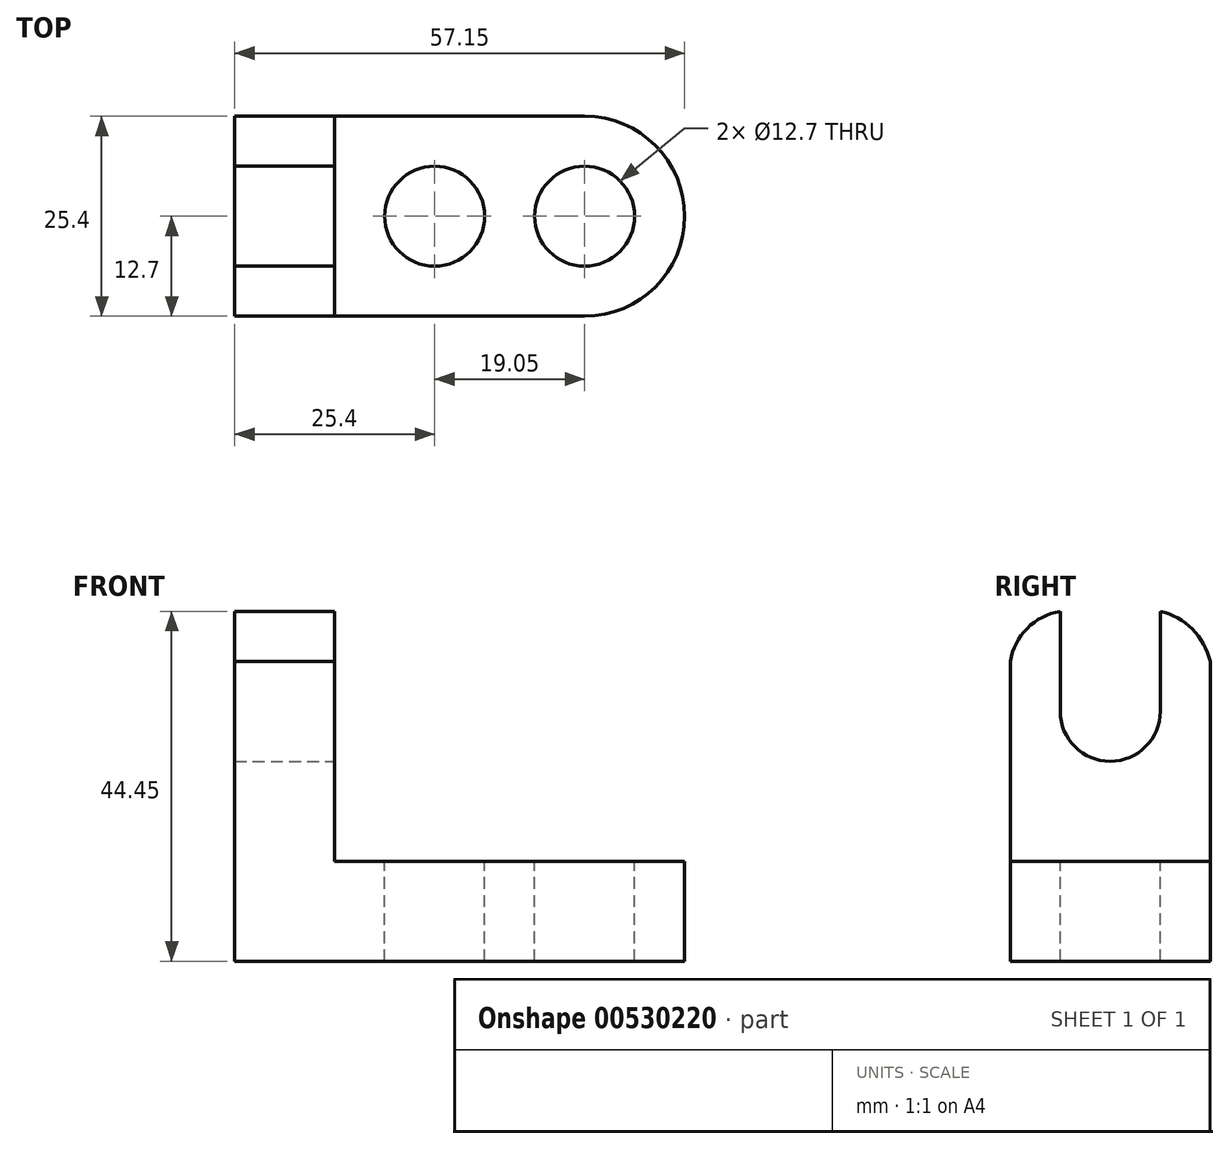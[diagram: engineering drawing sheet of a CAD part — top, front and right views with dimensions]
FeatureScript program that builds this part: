
annotation { "Feature Type Name" : "Feature", "Feature Type Description" : "" }
export const myFeature = defineFeature(function(context is Context, id is Id, definition is map)
    precondition{}
    {
        {
            var Q0;
            Q0=qCreatedBy(makeId("Front.planeOp"),FACE);
            var sketch = newSketch(context, id + "F0", { "sketchPlane" : qUnion([Q0])});
            skLineSegment(sketch, "E0", {"start": v(0, 0) * mm, "end": v(-44.45, 0) * mm});
            skLineSegment(sketch, "E1", {"start": v(-44.45, 0) * mm, "end": v(-44.45, 12.7) * mm});
            skLineSegment(sketch, "E2", {"start": v(-44.45, 12.7) * mm, "end": v(0, 12.7) * mm});
            skLineSegment(sketch, "E3", {"start": v(0, 12.7) * mm, "end": v(0, 0) * mm});
            skSolve(sketch);
        }
        {
            var Q0;
            Q0 = qSketchRegion(id + "F0", true);
            extrude(context, id + "F1", {"entities" : qUnion([Q0]), "depth" : 25.4 * mm, "offsetDistance" : 25.4 * mm});
        }
        {
            var Q0;
            Q0=makeQuery(id+"F1.opExtrude","SWEPT_FACE",FACE,{"disambiguationData":[OSD([sQuery(id+"F0.wireOp",EDGE,"E2")])]});
            var sketch = newSketch(context, id + "F2", { "sketchPlane" : qUnion([Q0])});
            skArc(sketch, "E4", {"start": v(0, -25.4) * mm, "mid": v(12.7, -12.7) * mm, "end": v(0, 0) * mm});
            skSolve(sketch);
        }
        {
            var Q0;
            Q0 = qSketchRegion(id + "F2", true);
            var Q1;
            Q1=makeQuery(id+"F2.imprint","IMPRINT",FACE,{"disambiguationData":[TD([[makeQuery(id+"F2.imprint","IMPRINT",EDGE,{"derivedFrom":sQuery(id+"F2.wireOp",EDGE,"E4")}),1.0]])]});
            extrude(context, id + "F3", {"entities" : qUnion([Q0, Q1]), "operationType" : NewBodyOperationType.ADD, "oppositeDirection" : true, "depth" : 12.7 * mm, "offsetDistance" : 25.4 * mm});
        }
        {
            var Q0;
            {var subQ0=sQuery(id+"F0.wireOp",EDGE,"E2");Q0=makeQuery(id+"F3.boolean.opBoolean","MERGE",FACE,{"derivedFrom":[makeQuery(id+"F1.opExtrude","SWEPT_FACE",FACE,{"disambiguationData":[OSD([subQ0])]}),makeQuery(id+"F3.opExtrude","CAP_FACE",FACE,{"disambiguationData":[OSD([subQ0,sQuery(id+"F0.wireOp",EDGE,"E3"),sQuery(id+"F2.wireOp",EDGE,"E4")])],"isStart":true})]});}
            var sketch = newSketch(context, id + "F4", { "sketchPlane" : qUnion([Q0])});
            skLineSegment(sketch, "E5", {"start": v(-31.75, 0) * mm, "end": v(-31.75, -25.4) * mm});
            skLineSegment(sketch, "E6", {"start": v(-31.75, -25.4) * mm, "end": v(-44.45, -25.4) * mm});
            skLineSegment(sketch, "E7", {"start": v(-44.45, -25.4) * mm, "end": v(-44.45, 0) * mm});
            skLineSegment(sketch, "E8", {"start": v(-44.45, 0) * mm, "end": v(-31.75, 0) * mm});
            skSolve(sketch);
        }
        {
            var Q0;
            Q0 = qSketchRegion(id + "F4", true);
            extrude(context, id + "F5", {"entities" : qUnion([Q0]), "operationType" : NewBodyOperationType.ADD, "depth" : 31.75 * mm, "offsetDistance" : 25.4 * mm});
        }
        {
            var Q0;
            Q0=makeQuery(id+"F5.opExtrude","SWEPT_FACE",FACE,{"disambiguationData":[OSD([sQuery(id+"F4.wireOp",EDGE,"E5")])]});
            var sketch = newSketch(context, id + "F6", { "sketchPlane" : qUnion([Q0])});
            skArc(sketch, "E9", {"start": v(-19.05, 44.45) * mm, "mid": v(-23.24, 42.3) * mm, "end": v(-25.4, 38.1) * mm});
            skArc(sketch, "E10", {"start": v(0, 38.1) * mm, "mid": v(-2.26, 42.19) * mm, "end": v(-6.35, 44.45) * mm});
            skSolve(sketch);
        }
        {
            var Q0;
            {var subQ4=sQuery(id+"F6.wireOp",EDGE,"Cz99WPWB-qGPV-rDuO-pkoG-oD4RdVajF85E");Q0=makeQuery(id+"F6.imprint","IMPRINT",FACE,{"disambiguationData":[TD([[makeQuery(id+"F6.imprint","IMPRINT",EDGE,{"derivedFrom":subQ4}),1.0]])]});}
            var sketch = newSketch(context, id + "F7", { "sketchPlane" : qUnion([Q0])});
            skSolve(sketch);
        }
        {
            var Q0;
            Q0 = qSketchRegion(id + "F6", true);
            var Q1;
            {var subQ0=sQuery(id+"F6.wireOp",EDGE,"E9");Q1=makeQuery(id+"F6.imprint","IMPRINT",FACE,{"disambiguationData":[TD([[makeQuery(id+"F6.imprint","IMPRINT",EDGE,{"derivedFrom":subQ0}),-1.0]])]});}
            var Q2;
            {var subQ0=sQuery(id+"F6.wireOp",EDGE,"E10");Q2=makeQuery(id+"F6.imprint","IMPRINT",FACE,{"disambiguationData":[TD([[makeQuery(id+"F6.imprint","IMPRINT",EDGE,{"derivedFrom":subQ0}),-1.0]])]});}
            extrude(context, id + "F8", {"entities" : qUnion([Q0, Q1, Q2]), "operationType" : NewBodyOperationType.REMOVE, "oppositeDirection" : true, "depth" : 25.4 * mm, "offsetDistance" : 25.4 * mm});
        }
        {
            var Q0;
            Q0=makeQuery(id+"F5.opExtrude","SWEPT_FACE",FACE,{"disambiguationData":[OSD([sQuery(id+"F4.wireOp",EDGE,"E5")])]});
            var sketch = newSketch(context, id + "F9", { "sketchPlane" : qUnion([Q0])});
            skLineSegment(sketch, "E11", {"start": v(-19.05, 44.45) * mm, "end": v(-19.05, 31.75) * mm});
            skLineSegment(sketch, "E12", {"start": v(-19.05, 31.75) * mm, "end": v(-6.35, 31.75) * mm});
            skLineSegment(sketch, "E13", {"start": v(-6.35, 31.75) * mm, "end": v(-6.35, 44.45) * mm});
            skLineSegment(sketch, "E14", {"start": v(-6.35, 44.45) * mm, "end": v(-19.05, 44.45) * mm});
            skArc(sketch, "E15", {"start": v(-19.05, 31.75) * mm, "mid": v(-12.7, 25.4) * mm, "end": v(-6.35, 31.75) * mm});
            skSolve(sketch);
        }
        {
            var Q0;
            Q0 = qSketchRegion(id + "F9", true);
            extrude(context, id + "F10", {"entities" : qUnion([Q0]), "operationType" : NewBodyOperationType.REMOVE, "oppositeDirection" : true, "depth" : 25.4 * mm, "offsetDistance" : 25.4 * mm});
        }
        {
            var Q0;
            {var subQ0=sQuery(id+"F0.wireOp",EDGE,"E2");Q0=makeQuery(id+"F3.boolean.opBoolean","MERGE",FACE,{"derivedFrom":[makeQuery(id+"F1.opExtrude","SWEPT_FACE",FACE,{"disambiguationData":[OSD([subQ0])]}),makeQuery(id+"F3.opExtrude","CAP_FACE",FACE,{"disambiguationData":[OSD([subQ0,sQuery(id+"F0.wireOp",EDGE,"E3"),sQuery(id+"F2.wireOp",EDGE,"E4")])],"isStart":true})]});}
            var sketch = newSketch(context, id + "F11", { "sketchPlane" : qUnion([Q0])});
            skCircle(sketch, "E16", {"center": v(0, -12.7) * mm, "radius": 6.35 * mm});
            skCircle(sketch, "E17", {"center": v(-19.05, -12.7) * mm, "radius": 6.35 * mm});
            skSolve(sketch);
        }
        {
            var Q0;
            Q0 = qSketchRegion(id + "F11", true);
            extrude(context, id + "F12", {"entities" : qUnion([Q0]), "operationType" : NewBodyOperationType.REMOVE, "oppositeDirection" : true, "depth" : 25.4 * mm, "offsetDistance" : 25.4 * mm});
        }
    });
